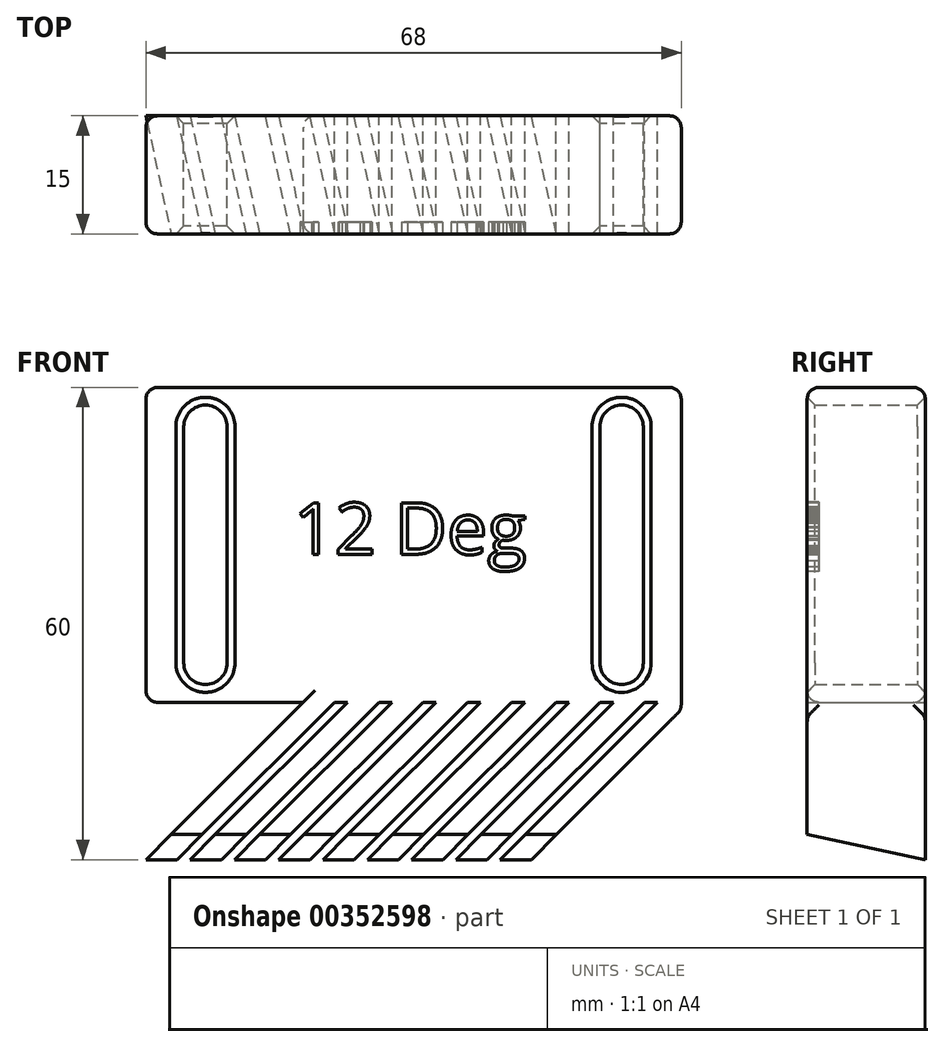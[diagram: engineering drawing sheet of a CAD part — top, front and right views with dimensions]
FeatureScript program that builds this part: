
annotation { "Feature Type Name" : "Feature", "Feature Type Description" : "" }
export const myFeature = defineFeature(function(context is Context, id is Id, definition is map)
    precondition{}
    {
        {
            var Q0;
            Q0=qCreatedBy(makeId("Front.planeOp"),FACE);
            var sketch = newSketch(context, id + "F0", { "sketchPlane" : qUnion([Q0])});
            skLineSegment(sketch, "E0.top", {"start": v(34, 30) * mm, "end": v(-34, 30) * mm});
            skLineSegment(sketch, "E0.left", {"start": v(34, -10.96) * mm, "end": v(34, 30) * mm});
            skLineSegment(sketch, "E0.right", {"start": v(-34, -10) * mm, "end": v(-34, 30) * mm});
            skPoint(sketch, "E0.middle", {"position": v(0, 0) * mm});
            skLineSegment(sketch, "E1", {"start": v(-34, -30) * mm, "end": v(-14, -10) * mm});
            skLineSegment(sketch, "E2", {"start": v(-10.04, -10) * mm, "end": v(-30.04, -30) * mm});
            skLineSegment(sketch, "E3.1.0.0", {"start": v(-28.38, -30) * mm, "end": v(-8.37, -10) * mm});
            skLineSegment(sketch, "E3.1.0.1", {"start": v(-4.42, -10) * mm, "end": v(-24.42, -30) * mm});
            skLineSegment(sketch, "E3.2.0.0", {"start": v(-22.75, -30) * mm, "end": v(-2.75, -10) * mm});
            skLineSegment(sketch, "E3.2.0.1", {"start": v(1.2, -10) * mm, "end": v(-18.8, -30) * mm});
            skLineSegment(sketch, "E3.3.0.0", {"start": v(-17.12, -30) * mm, "end": v(2.88, -10) * mm});
            skLineSegment(sketch, "E3.3.0.1", {"start": v(6.83, -10) * mm, "end": v(-13.17, -30) * mm});
            skLineSegment(sketch, "E3.4.0.0", {"start": v(-11.5, -30) * mm, "end": v(8.5, -10) * mm});
            skLineSegment(sketch, "E3.4.0.1", {"start": v(12.46, -10) * mm, "end": v(-7.54, -30) * mm});
            skLineSegment(sketch, "E3.5.0.0", {"start": v(-5.87, -30) * mm, "end": v(14.13, -10) * mm});
            skLineSegment(sketch, "E3.5.0.1", {"start": v(18.08, -10) * mm, "end": v(-1.92, -30) * mm});
            skLineSegment(sketch, "E3.6.0.0", {"start": v(-0.25, -30) * mm, "end": v(19.75, -10) * mm});
            skLineSegment(sketch, "E3.6.0.1", {"start": v(23.7, -10) * mm, "end": v(3.7, -30) * mm});
            skLineSegment(sketch, "E3.7.0.0", {"start": v(5.38, -30) * mm, "end": v(25.38, -10) * mm});
            skLineSegment(sketch, "E3.7.0.1", {"start": v(29.33, -10) * mm, "end": v(9.33, -30) * mm});
            skLineSegment(sketch, "E3.8.0.0", {"start": v(11, -30) * mm, "end": v(31, -10) * mm});
            skLineSegment(sketch, "E3.8.0.1", {"start": v(34, -10.96) * mm, "end": v(14.96, -30) * mm});
            skLineSegment(sketch, "E3.direction1", {"start": v(-34, -30) * mm, "end": v(-30.04, -30) * mm, "construction": true});
            skLineSegment(sketch, "E4.trimOffspring", {"start": v(-24.42, -30) * mm, "end": v(-28.37, -30) * mm});
            skLineSegment(sketch, "E5.trimOffspring", {"start": v(-30.04, -30) * mm, "end": v(-34, -30) * mm});
            skLineSegment(sketch, "E6.trimOffspring", {"start": v(-18.8, -30) * mm, "end": v(-22.75, -30) * mm});
            skLineSegment(sketch, "E7.trimOffspring", {"start": v(-13.17, -30) * mm, "end": v(-17.12, -30) * mm});
            skLineSegment(sketch, "E8.trimOffspring", {"start": v(-7.54, -30) * mm, "end": v(-11.5, -30) * mm});
            skLineSegment(sketch, "E9.trimOffspring", {"start": v(-1.92, -30) * mm, "end": v(-5.87, -30) * mm});
            skLineSegment(sketch, "E10.trimOffspring", {"start": v(3.7, -30) * mm, "end": v(-0.25, -30) * mm});
            skLineSegment(sketch, "E11.trimOffspring", {"start": v(9.33, -30) * mm, "end": v(5.38, -30) * mm});
            skLineSegment(sketch, "E12.trimOffspring", {"start": v(14.96, -30) * mm, "end": v(11, -30) * mm});
            skPoint(sketch, "E13.orphan", {"position": v(20.58, -30) * mm});
            skPoint(sketch, "E14.orphan", {"position": v(34, -30) * mm});
            skLineSegment(sketch, "E15", {"start": v(-10.04, -10) * mm, "end": v(-8.37, -10) * mm});
            skLineSegment(sketch, "E16.trimOffspring", {"start": v(-4.42, -10) * mm, "end": v(-2.75, -10) * mm});
            skLineSegment(sketch, "E17.trimOffspring", {"start": v(1.2, -10) * mm, "end": v(2.88, -10) * mm});
            skLineSegment(sketch, "E18.trimOffspring", {"start": v(6.83, -10) * mm, "end": v(8.5, -10) * mm});
            skLineSegment(sketch, "E19.trimOffspring", {"start": v(12.46, -10) * mm, "end": v(14.13, -10) * mm});
            skLineSegment(sketch, "E20.trimOffspring", {"start": v(18.08, -10) * mm, "end": v(19.75, -10) * mm});
            skLineSegment(sketch, "E21.trimOffspring", {"start": v(23.7, -10) * mm, "end": v(25.38, -10) * mm});
            skLineSegment(sketch, "E22", {"start": v(-14, -10) * mm, "end": v(-34, -10) * mm});
            skArc(sketch, "E23.0.startCap", {"start": v(-29.19, 25) * mm, "mid": v(-26.44, 27.75) * mm, "end": v(-23.69, 25) * mm});
            skArc(sketch, "E23.0.endCap", {"start": v(-23.69, -5) * mm, "mid": v(-26.44, -7.75) * mm, "end": v(-29.19, -5) * mm});
            skLineSegment(sketch, "E23.0.left", {"start": v(-23.69, 25) * mm, "end": v(-23.69, -5) * mm});
            skLineSegment(sketch, "E23.0.right", {"start": v(-29.19, 25) * mm, "end": v(-29.19, -5) * mm});
            skLineSegment(sketch, "E24.MirrorCS", {"start": v(23.69, 25) * mm, "end": v(23.69, -5) * mm});
            skLineSegment(sketch, "E25.MirrorCS", {"start": v(29.19, 25) * mm, "end": v(29.19, -5) * mm});
            skArc(sketch, "E26.MirrorCS", {"start": v(29.19, 25) * mm, "mid": v(26.44, 27.75) * mm, "end": v(23.69, 25) * mm});
            skArc(sketch, "E27.MirrorCS", {"start": v(23.69, -5) * mm, "mid": v(26.44, -7.75) * mm, "end": v(29.19, -5) * mm});
            skLineSegment(sketch, "E28", {"start": v(29.33, -10) * mm, "end": v(31, -10) * mm});
            skPoint(sketch, "E29.orphan", {"position": v(34.96, -10) * mm});
            skSolve(sketch);
        }
        {
            var Q0;
            Q0=qSketchRegion(id+"F0",true);
            extrude(context, id + "F1", {"entities" : qUnion([Q0]), "depth" : 15 * mm});
        }
        {
            var Q0;
            Q0=makeQuery(id+"F1.opExtrude","CAP_EDGE",EDGE,{"disambiguationData":[OSD([sQuery(id+"F0.wireOp",EDGE,"E23.0.right")])],"isStart":false});
            var Q1;
            Q1=makeQuery(id+"F1.opExtrude","CAP_EDGE",EDGE,{"disambiguationData":[OSD([sQuery(id+"F0.wireOp",EDGE,"E23.0.left")])],"isStart":true});
            var Q2;
            Q2=makeQuery(id+"F1.opExtrude","CAP_EDGE",EDGE,{"disambiguationData":[OSD([sQuery(id+"F0.wireOp",EDGE,"E25.MirrorCS")])],"isStart":true});
            var Q3;
            Q3=makeQuery(id+"F1.opExtrude","CAP_EDGE",EDGE,{"disambiguationData":[OSD([sQuery(id+"F0.wireOp",EDGE,"E25.MirrorCS")])],"isStart":false});
            chamfer(context, id + "F2", {"entities" : qUnion([Q0, Q1, Q2, Q3]), "width" : 1 * mm, "tangentPropagation" : true});
        }
        {
            var Q0;
            Q0=makeQuery(id+"F1.opExtrude","CAP_EDGE",EDGE,{"disambiguationData":[OSD([sQuery(id+"F0.wireOp",EDGE,"E0.top")])],"isStart":false});
            var Q1;
            Q1=makeQuery(id+"F1.opExtrude","CAP_EDGE",EDGE,{"disambiguationData":[OSD([sQuery(id+"F0.wireOp",EDGE,"E0.right")])],"isStart":false});
            var Q2;
            Q2=makeQuery(id+"F1.opExtrude","CAP_EDGE",EDGE,{"disambiguationData":[OSD([sQuery(id+"F0.wireOp",EDGE,"E0.right")])],"isStart":true});
            var Q3;
            Q3=makeQuery(id+"F1.opExtrude","CAP_EDGE",EDGE,{"disambiguationData":[OSD([sQuery(id+"F0.wireOp",EDGE,"E22")])],"isStart":false});
            var Q4;
            Q4=makeQuery(id+"F1.opExtrude","CAP_EDGE",EDGE,{"disambiguationData":[OSD([sQuery(id+"F0.wireOp",EDGE,"E22")])],"isStart":true});
            var Q5;
            Q5=makeQuery(id+"F1.opExtrude","CAP_EDGE",EDGE,{"disambiguationData":[OSD([sQuery(id+"F0.wireOp",EDGE,"E0.left")])],"isStart":false});
            var Q6;
            Q6=makeQuery(id+"F1.opExtrude","SWEPT_EDGE",EDGE,{"disambiguationData":[OSD([sQuery(id+"F0.wireOp",EDGE,"E0.top"),sQuery(id+"F0.wireOp",EDGE,"E0.left")])]});
            var Q7;
            Q7=makeQuery(id+"F1.opExtrude","SWEPT_EDGE",EDGE,{"disambiguationData":[OSD([sQuery(id+"F0.wireOp",EDGE,"E0.left"),sQuery(id+"F0.wireOp",EDGE,"E3.8.0.1")])]});
            var Q8;
            Q8=makeQuery(id+"F1.opExtrude","CAP_EDGE",EDGE,{"disambiguationData":[OSD([sQuery(id+"F0.wireOp",EDGE,"E0.left")])],"isStart":true});
            var Q9;
            Q9=makeQuery(id+"F1.opExtrude","CAP_EDGE",EDGE,{"disambiguationData":[OSD([sQuery(id+"F0.wireOp",EDGE,"E0.top")])],"isStart":true});
            fillet(context, id + "F3", {"entities" : qUnion([Q0, Q1, Q2, Q3, Q4, Q5, Q6, Q7, Q8, Q9]), "radius" : 1.5 * mm, "tangentPropagation" : true, "allowEdgeOverflow" : false});
        }
        {
            var Q0;
            Q0=qCreatedBy(makeId("Right.planeOp"),FACE);
            var sketch = newSketch(context, id + "F4", { "sketchPlane" : qUnion([Q0])});
            skLineSegment(sketch, "E30", {"start": v(0, -30) * mm, "end": v(-15, -30) * mm});
            skLineSegment(sketch, "E31", {"start": v(-15, -30) * mm, "end": v(-15, -26.81) * mm});
            skLineSegment(sketch, "E32", {"start": v(-15, -26.81) * mm, "end": v(0, -30) * mm});
            skSolve(sketch);
        }
        {
            var Q0;
            Q0 = qSketchRegion(id + "F4", true);
            extrude(context, id + "F5", {"entities" : qUnion([Q0]), "operationType" : NewBodyOperationType.REMOVE, "oppositeDirection" : true, "depth" : 70 * mm, "symmetric" : true});
        }
        {
            var Q0;
            Q0=makeQuery(id+"F1.opExtrude","SWEPT_EDGE",EDGE,{"disambiguationData":[OSD([sQuery(id+"F0.wireOp",EDGE,"E0.top"),sQuery(id+"F0.wireOp",EDGE,"E0.right")])]});
            var Q1;
            Q1=makeQuery(id+"F1.opExtrude","SWEPT_EDGE",EDGE,{"disambiguationData":[OSD([sQuery(id+"F0.wireOp",EDGE,"E0.right"),sQuery(id+"F0.wireOp",EDGE,"E22")])]});
            fillet(context, id + "F6", {"entities" : qUnion([Q0, Q1]), "radius" : 1.5 * mm, "tangentPropagation" : true, "allowEdgeOverflow" : false});
        }
        {
            var Q0;
            Q0=makeQuery(id+"F3.opFillet","SPLIT",FACE,{"disambiguationData":[OD(1.0)],"derivedFrom":makeQuery(id+"F1.opExtrude","CAP_FACE",FACE,{"disambiguationData":[OSD([sQuery(id+"F0.wireOp",EDGE,"E0.top"),sQuery(id+"F0.wireOp",EDGE,"E0.left"),sQuery(id+"F0.wireOp",EDGE,"E0.right"),sQuery(id+"F0.wireOp",EDGE,"E1"),sQuery(id+"F0.wireOp",EDGE,"E2"),sQuery(id+"F0.wireOp",EDGE,"E3.1.0.0"),sQuery(id+"F0.wireOp",EDGE,"E3.1.0.1"),sQuery(id+"F0.wireOp",EDGE,"E3.2.0.0"),sQuery(id+"F0.wireOp",EDGE,"E3.2.0.1"),sQuery(id+"F0.wireOp",EDGE,"E3.3.0.0"),sQuery(id+"F0.wireOp",EDGE,"E3.3.0.1"),sQuery(id+"F0.wireOp",EDGE,"E3.4.0.0"),sQuery(id+"F0.wireOp",EDGE,"E3.4.0.1"),sQuery(id+"F0.wireOp",EDGE,"E3.5.0.0"),sQuery(id+"F0.wireOp",EDGE,"E3.5.0.1"),sQuery(id+"F0.wireOp",EDGE,"E3.6.0.0"),sQuery(id+"F0.wireOp",EDGE,"E3.6.0.1"),sQuery(id+"F0.wireOp",EDGE,"E3.7.0.0"),sQuery(id+"F0.wireOp",EDGE,"E3.7.0.1"),sQuery(id+"F0.wireOp",EDGE,"E3.8.0.0"),sQuery(id+"F0.wireOp",EDGE,"E3.8.0.1"),sQuery(id+"F0.wireOp",EDGE,"E4.trimOffspring"),sQuery(id+"F0.wireOp",EDGE,"E5.trimOffspring"),sQuery(id+"F0.wireOp",EDGE,"E6.trimOffspring"),sQuery(id+"F0.wireOp",EDGE,"E7.trimOffspring"),sQuery(id+"F0.wireOp",EDGE,"E8.trimOffspring"),sQuery(id+"F0.wireOp",EDGE,"E9.trimOffspring"),sQuery(id+"F0.wireOp",EDGE,"E10.trimOffspring"),sQuery(id+"F0.wireOp",EDGE,"E11.trimOffspring"),sQuery(id+"F0.wireOp",EDGE,"E12.trimOffspring"),sQuery(id+"F0.wireOp",EDGE,"E15"),sQuery(id+"F0.wireOp",EDGE,"E16.trimOffspring"),sQuery(id+"F0.wireOp",EDGE,"E17.trimOffspring"),sQuery(id+"F0.wireOp",EDGE,"E18.trimOffspring"),sQuery(id+"F0.wireOp",EDGE,"E19.trimOffspring"),sQuery(id+"F0.wireOp",EDGE,"E20.trimOffspring"),sQuery(id+"F0.wireOp",EDGE,"E21.trimOffspring"),sQuery(id+"F0.wireOp",EDGE,"E22"),sQuery(id+"F0.wireOp",EDGE,"E23.0.startCap"),sQuery(id+"F0.wireOp",EDGE,"E23.0.endCap"),sQuery(id+"F0.wireOp",EDGE,"E23.0.left"),sQuery(id+"F0.wireOp",EDGE,"E23.0.right"),sQuery(id+"F0.wireOp",EDGE,"E24.MirrorCS"),sQuery(id+"F0.wireOp",EDGE,"E25.MirrorCS"),sQuery(id+"F0.wireOp",EDGE,"E26.MirrorCS"),sQuery(id+"F0.wireOp",EDGE,"E27.MirrorCS"),sQuery(id+"F0.wireOp",EDGE,"E28")])],"isStart":false})});
            var sketch = newSketch(context, id + "F7", { "sketchPlane" : qUnion([Q0])});
            skText(sketch, "E33", { "text": "12 Deg", "fontName": "OpenSans-Regular.ttf"});
            const initialGuessF7  = {"E33": [-0.01524, 0.0088, 1, 0, 0.00658]};
            skSetInitialGuess(sketch, initialGuessF7);
            skSolve(sketch);
        }
        {
            var Q0;
            Q0 = qSketchRegion(id + "F7", true);
            extrude(context, id + "F8", {"entities" : qUnion([Q0]), "operationType" : NewBodyOperationType.REMOVE, "oppositeDirection" : true, "depth" : 1.5 * mm});
        }
    });
